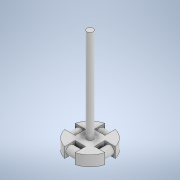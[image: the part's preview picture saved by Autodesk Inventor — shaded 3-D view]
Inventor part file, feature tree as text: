
AUTODESK INVENTOR PART (.ipt)
format: ipt  version: 2021 (Build 250183000, 183)  size: 150,528 bytes
history: native  units: mm
features: extrude x3, sketch x3, pattern_circular x1
ambient origin geometry x8: Origin, YZ Plane, XZ Plane, XY Plane, X Axis, Y Axis, Z Axis, Center Point
bodies: Solid1 (feature_tree)
feature tree (7):
  extrude  "Extrusion1"  Depth=3.33mm
  extrude  "Extrusion2"  Depth=3.33mm TaperAngle=0.0deg
  pattern_circular  "Circular Pattern1"  [2 undecoded]
  extrude  "Extrusion3"  Depth=30.0mm TaperAngle=360.0deg
  sketch  "Sketch1"  dims[d0=13.33mm d1=3.33mm]
  sketch  "Sketch2"  dims[d2=40.0mm d4=360.0deg d6=3.33mm d7=0.0mm]
  sketch  "Sketch3"  dims[d8=2.66mm d9=3.33mm d10=0.0mm d11=40.0mm d12=360.0deg d14=2.0mm d15=30.0mm d16=0.0mm]
note: 2 required parameter values undecoded (feature->parameter linkage not recoverable at this tier; creation-order binding heuristic only, values carry confidence <= 0.55)
